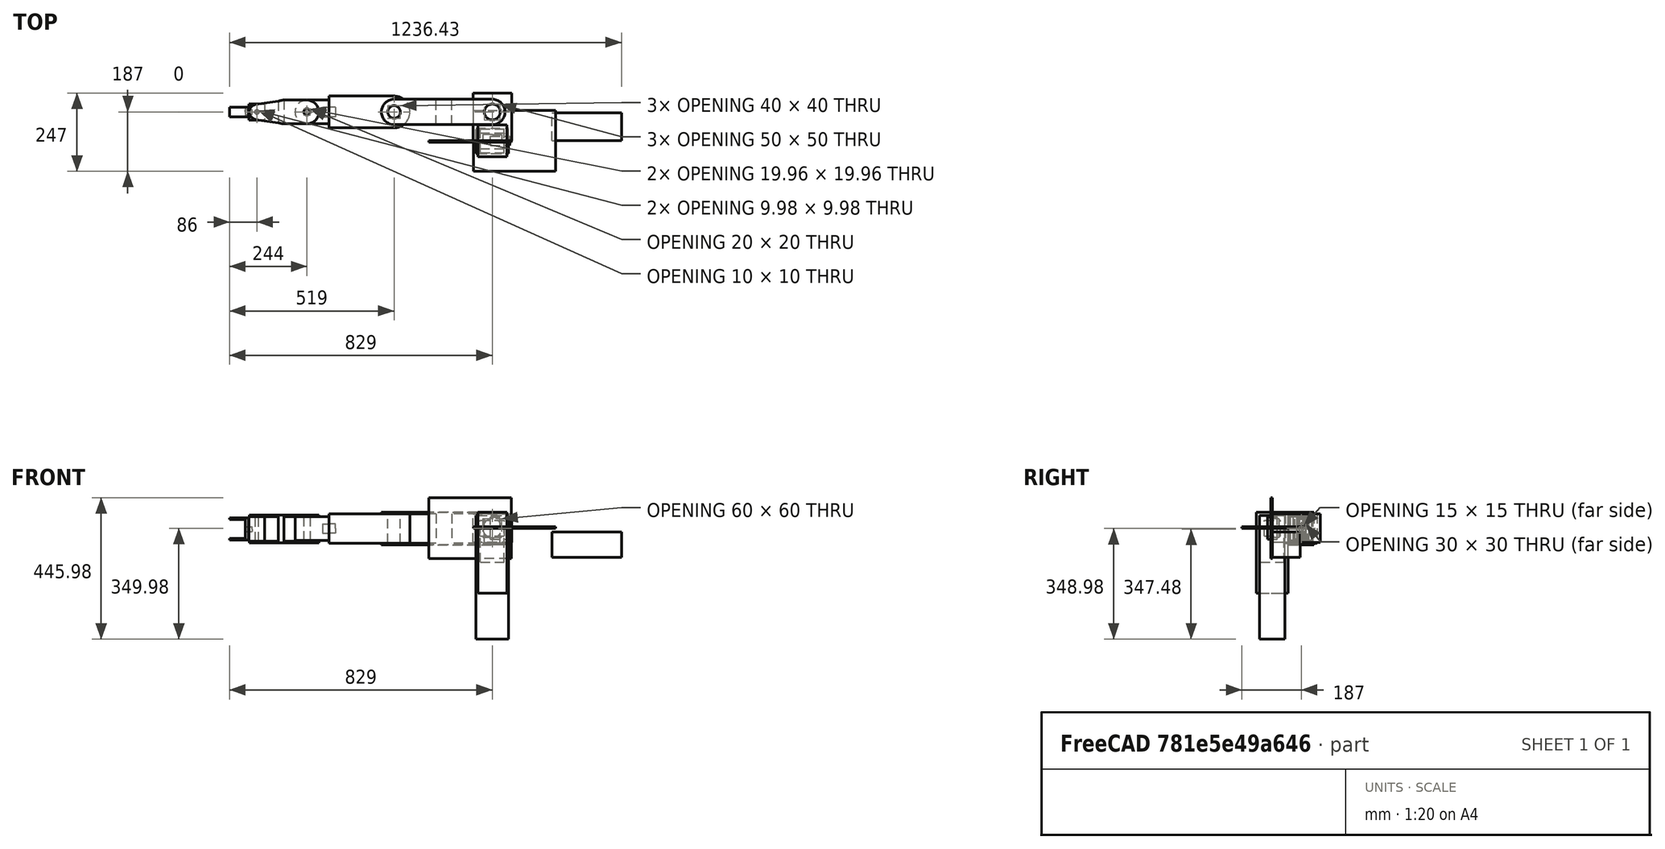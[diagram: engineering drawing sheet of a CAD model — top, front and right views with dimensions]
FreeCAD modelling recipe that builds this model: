
FCSTD DOCUMENT  (FreeCAD 1.0R39109 (Git))
Label: Arm_CAD
License: All rights reserved
LicenseURL: https://en.wikipedia.org/wiki/All_rights_reserved
objects: App::Link×24, App::Part×17, App::FeaturePython×15, Part::Feature×8, Part::Box×8, App::DocumentObjectGroup×1, App::DocumentObjectGroupPython×1
note: 16 computed .brp shape members not serialized (recipe doc carries the construction recipe); baked Part::Feature solids carry a one-line shape summary decoded from their .brp

FEATURE [Part::Feature] Part__Feature  label="Link0"
  shape: bbox 122 x 151 x 90 mm, 11 faces (baked)
FEATURE [Part::Feature] Part__Feature001  label="Link1"
  Placement = pos=(2.26e-14,91,-1.25) rot=(0,1,0;1.5708rad)
  shape: bbox 390 x 80 x 102.5 mm, 24 faces (baked)
FEATURE [Part::Feature] Part__Feature002  label="Link2"
  Placement = pos=(-310,91,-1) rot=(0.707107,0,0.707107;3.14159rad)
  shape: bbox 255 x 100 x 92 mm, 12 faces (baked)
FEATURE [Part::Feature] Part__Feature003  label="Link3"
  Placement = pos=(-515,91,-1) rot=(0,1,0;1.5708rad)
  shape: bbox 107.5 x 75 x 75 mm, 11 faces (baked)
FEATURE [Part::Feature] Part__Feature004  label="Base"
  Placement = pos=(-1.822e-13,-5,-2.788e-13) rot=(0,0.707107,0.707107;3.14159rad)
  shape: bbox 260 x 5 x 192 mm, 8 faces (baked)
FEATURE [Part::Feature] Part__Feature005  label="Link4"
  Placement = pos=(-957.544,122.197,41.5) rot=(-0.999068,-0.030524,0.030524;1.57173rad)
  shape: bbox 219.5 x 75 x 88 mm, 36 faces (baked)
FEATURE [Part::Feature] Part__Feature006  label="Link5"
  Placement = pos=(-743,91,-2.5) rot=(0,1,0;1.5708rad)
  shape: bbox 50 x 50 x 78 mm, 11 faces (baked)
FEATURE [Part::Feature] Part__Feature007  label="Claw"
  Placement = pos=(-774,91,-2.5) rot=(0,1,0;3.14159rad)
  shape: bbox 61 x 30 x 70 mm, 16 faces (baked)
FEATURE [App::Link] Base001  label="Base002"
  LinkedObject = -> Part__Feature004
FEATURE [App::Part] Base  label="Base001"
  Group = -> [Base001]
  Origin = -> Origin001
FEATURE [App::Link] real_l_Base001_
  LinkedObject = -> Base
FEATURE [App::Link] Link001
  LinkedObject = -> Part__Feature
FEATURE [App::Part] Link0  label="Link006"
  Group = -> [Link001]
  Origin = -> Origin002
FEATURE [App::Link] Link002
  LinkedObject = -> Part__Feature001
FEATURE [App::Part] Link1  label="Link007"
  Group = -> [Link002]
  Origin = -> Origin003
FEATURE [App::Link] Link003
  LinkedObject = -> Part__Feature002
FEATURE [App::Part] Link2  label="Link008"
  Group = -> [Link003]
  Origin = -> Origin004
FEATURE [App::Link] Link004
  LinkedObject = -> Part__Feature003
FEATURE [App::Part] Link3  label="Link009"
  Group = -> [Link004]
  Origin = -> Origin005
FEATURE [App::Link] Link005
  LinkedObject = -> Part__Feature005
FEATURE [App::Part] Link4  label="Link010"
  Group = -> [Link005]
  Origin = -> Origin006
FEATURE [App::Link] Link006  label="Link012"
  LinkedObject = -> Part__Feature006
FEATURE [App::Part] Link5  label="Link011"
  Group = -> [Link006]
  Origin = -> Origin007
FEATURE [App::Link] Claw001  label="Claw002"
  LinkedObject = -> Part__Feature007
FEATURE [App::Part] Claw  label="Claw001"
  Group = -> [Claw001]
  Origin = -> Origin008
FEATURE [App::Part] _X2_88c5914d4f53_X0_  label="Arm_asm"
  Group = -> [Part__Feature007,Part__Feature006,Part__Feature005,Part__Feature003,Part__Feature002,Part__Feature001,Part__Feature,Part__Feature004,Base,Link0,Link1,Link2,Link3,Link4,Link5,Claw]
  Origin = -> Origin
FEATURE [App::FeaturePython] l_Base001__to__l_Link006  # WARN: FeaturePython — macro-defined, semantics opaque (R4)
  Child = 1
  Effort = 0
  JoinRotationDirection = 0
  JointSpecific = 0
  LowerLimit = -180
  Mimic = false
  Multiplier = 1
  Origin = pos=(-6e-16,9e-16,5) rot=(1,0,0;3.14159rad)
  Parent = 1
  Placement = pos=(-6e-16,9e-16,5) rot=(1,0,0;3.14159rad)
  Position = 0
  Type = 2
  UpperLimit = 180
  Velocity = 180
  _Type = Cross::Joint
FEATURE [App::FeaturePython] l_Link006__to__l_Link007  # WARN: FeaturePython — macro-defined, semantics opaque (R4)
  Child = 1
  Effort = 0
  JoinRotationDirection = 0
  JointSpecific = 0
  LowerLimit = -90
  Mimic = false
  Multiplier = 1
  Origin = pos=(0,45,-91) rot=(-1,0,0;4.71239rad)
  Parent = 2
  Placement = pos=(1.76e-14,-45,96) rot=(-1,0,0;1.5708rad)
  Position = 0
  Type = 2
  UpperLimit = 90
  Velocity = 180
  _Type = Cross::Joint
FEATURE [App::FeaturePython] l_Link007__to__l_Link008  # WARN: FeaturePython — macro-defined, semantics opaque (R4)
  Child = 1
  Effort = 0
  JoinRotationDirection = 0
  JointSpecific = 0
  LowerLimit = -90
  Mimic = false
  Multiplier = 1
  Origin = pos=(1.67e-14,-310,92.5) rot=(0,-1,0;3.14159rad)
  Parent = 3
  Placement = pos=(9.63e-14,47.5,406) rot=(0,-0.707107,0.707107;3.14159rad)
  Position = 0
  Type = 2
  UpperLimit = 90
  Velocity = 180
  _Type = Cross::Joint
FEATURE [App::FeaturePython] l_Link008__to__l_Link009  # WARN: FeaturePython — macro-defined, semantics opaque (R4)
  Child = 1
  Effort = 0
  JoinRotationDirection = 0
  JointSpecific = 0
  LowerLimit = -180
  Mimic = false
  Multiplier = 1
  Origin = pos=(1.4133e-12,-205,46) rot=(-0.57735,-0.57735,-0.57735;2.0944rad)
  Parent = 4
  Placement = pos=(-1.3841e-12,1.5,611) rot=(0.707107,-0.707107,0;3.14159rad)
  Position = 0
  Type = 2
  UpperLimit = 180
  Velocity = 180
  _Type = Cross::Joint
FEATURE [App::FeaturePython] l_Link009__to__l_Link010  # WARN: FeaturePython — macro-defined, semantics opaque (R4)
  Child = 1
  Effort = 0
  JoinRotationDirection = 0
  JointSpecific = 0
  LowerLimit = -180
  Mimic = false
  Multiplier = 1
  Origin = pos=(37.5,-4.277e-13,-70) rot=(-0.57735,-0.57735,0.57735;2.0944rad)
  Parent = 5
  Placement = pos=(-1.4753e-12,-36,681) rot=(0,-0.707107,-0.707107;3.14159rad)
  Position = 0
  Type = 2
  UpperLimit = 0
  Velocity = 180
  _Type = Cross::Joint
FEATURE [App::FeaturePython] l_Link010__to__l_Link011  # WARN: FeaturePython — macro-defined, semantics opaque (R4)
  Child = 1
  Effort = 0
  JoinRotationDirection = 0
  JointSpecific = 0
  LowerLimit = -90
  Mimic = false
  Multiplier = 1
  Origin = pos=(-157.705,-9.64567,78) rot=(0,0,1;0rad)
  Parent = 6
  Placement = pos=(157.705,42,671.354) rot=(0,-0.707107,-0.707107;3.14159rad)
  Position = 0
  Type = 2
  UpperLimit = 90
  Velocity = 180
  _Type = Cross::Joint
FEATURE [App::FeaturePython] l_Link011__to__l_Claw001  # WARN: FeaturePython — macro-defined, semantics opaque (R4)
  Child = 1
  Effort = 0
  JoinRotationDirection = 0
  JointSpecific = 0
  LowerLimit = -180
  Mimic = false
  Multiplier = 1
  Origin = pos=(-25,-3.411e-13,-39) rot=(0.707107,0,0.707107;3.14159rad)
  Parent = 7
  Placement = pos=(182.705,3,671.354) rot=(-0.57735,-0.57735,0.57735;2.0944rad)
  Position = 0
  Type = 2
  UpperLimit = 180
  Velocity = 180
  _Type = Cross::Joint
FEATURE [App::Link] real_l_Claw001_
  LinkPlacement = pos=(188.705,3,671.354) rot=(-1,0,0;1.5708rad)
  LinkedObject = -> Claw
  Placement = pos=(188.705,3,671.354) rot=(-1,0,0;1.5708rad)
FEATURE [App::Link] real_l_Link011_
  LinkPlacement = pos=(157.705,3,671.354) rot=(-0.57735,-0.57735,0.57735;2.0944rad)
  LinkedObject = -> Link5
  Placement = pos=(157.705,3,671.354) rot=(-0.57735,-0.57735,0.57735;2.0944rad)
FEATURE [App::Link] real_l_Link010_
  LinkPlacement = pos=(369.945,-41,627.118) rot=(0,-1,0;3.14159rad)
  LinkedObject = -> Link4
  Placement = pos=(369.945,-41,627.118) rot=(0,-1,0;3.14159rad)
FEATURE [App::Link] real_l_Link009_
  LinkPlacement = pos=(-9.294e-13,1.5,611) rot=(0.707107,-0.707107,0;3.14159rad)
  LinkedObject = -> Link3
  Placement = pos=(-9.294e-13,1.5,611) rot=(0.707107,-0.707107,0;3.14159rad)
FEATURE [App::Link] real_l_Link008_
  LinkPlacement = pos=(6e-14,1.5,406) rot=(0.707107,-0.707107,0;3.14159rad)
  LinkedObject = -> Link2
  Placement = pos=(6e-14,1.5,406) rot=(0.707107,-0.707107,0;3.14159rad)
FEATURE [App::Link] real_l_Link007_
  LinkPlacement = pos=(3.81e-14,1.25,96) rot=(-0.707107,-0.707107,0;3.14159rad)
  LinkedObject = -> Link1
  Placement = pos=(3.81e-14,1.25,96) rot=(-0.707107,-0.707107,0;3.14159rad)
FEATURE [App::Link] real_l_Link006_
  LinkPlacement = pos=(-6e-16,9e-16,5) rot=(1,0,0;1.5708rad)
  LinkedObject = -> Link0
  Placement = pos=(-6e-16,9e-16,5) rot=(1,0,0;1.5708rad)
FEATURE [Part::Box] col_Base__BoundBox
  AttacherType = Attacher::AttachEngine3D
  Height = 5
  Length = 260
  Placement = pos=(-60,-96,-9e-16) rot=(0,0,1;0rad)
  Width = 192
FEATURE [App::Part] col__l_Base001__col_Base__BoundBox
  Group = -> [col_Base__BoundBox]
  Origin = -> Origin009
FEATURE [App::Link] collision_l_Base001_
  LinkedObject = -> col__l_Base001__col_Base__BoundBox
FEATURE [App::FeaturePython] l_Base001  # WARN: FeaturePython — macro-defined, semantics opaque (R4)
  CalculateInertiaBasedOnMass = false
  Collision = -> [col__l_Base001__col_Base__BoundBox]
  Group = -> [real_l_Base001_,collision_l_Base001_]
  Ixx = 0
  Ixy = 0
  Ixz = 0
  Iyy = 0
  Iyz = 0
  Izz = 0
  Mass = 0
  MaterialNotCalculate = false
  Real = -> [Base]
  Visual = -> [Base]
  _Type = Cross::Link
FEATURE [Part::Box] col_Link0__BoundBox
  AttacherType = Attacher::AttachEngine3D
  Height = 90
  Length = 122
  Placement = pos=(-61,0,-45) rot=(0,0,1;0rad)
  Width = 151
FEATURE [App::Part] col__l_Link006__col_Link0__BoundBox
  Group = -> [col_Link0__BoundBox]
  Origin = -> Origin010
  Placement = pos=(-6e-16,9e-16,5) rot=(1,0,0;1.5708rad)
FEATURE [App::Link] collision_l_Link006_
  LinkPlacement = pos=(-6e-16,9e-16,5) rot=(1,0,0;1.5708rad)
  LinkedObject = -> col__l_Link006__col_Link0__BoundBox
  Placement = pos=(-6e-16,9e-16,5) rot=(1,0,0;1.5708rad)
FEATURE [App::FeaturePython] l_Link006  # WARN: FeaturePython — macro-defined, semantics opaque (R4)
  CalculateInertiaBasedOnMass = false
  Collision = -> [col__l_Link006__col_Link0__BoundBox]
  Group = -> [real_l_Link006_,collision_l_Link006_]
  Ixx = 0
  Ixy = 0
  Ixz = 0
  Iyy = 0
  Iyz = 0
  Izz = 0
  Mass = 0
  MaterialNotCalculate = false
  MountedPlacement = pos=(0,0,0) rot=(-1,0,0;1.5708rad)
  Placement = pos=(-6e-16,9e-16,5) rot=(1,0,0;1.5708rad)
  Real = -> [Link0]
  Visual = -> [Link0]
  _Type = Cross::Link
FEATURE [Part::Box] col_Link1__BoundBox
  AttacherType = Attacher::AttachEngine3D
  Height = 389.985
  Length = 102.5
  Placement = pos=(-51.25,-40,-349.985) rot=(0,0,1;0rad)
  Width = 80
FEATURE [App::Part] col__l_Link007__col_Link1__BoundBox
  Group = -> [col_Link1__BoundBox]
  Origin = -> Origin011
  Placement = pos=(3.42e-14,1.25,96) rot=(-0.707107,-0.707107,0;3.14159rad)
FEATURE [App::Link] collision_l_Link007_
  LinkPlacement = pos=(3.81e-14,1.25,96) rot=(-0.707107,-0.707107,0;3.14159rad)
  LinkedObject = -> col__l_Link007__col_Link1__BoundBox
  Placement = pos=(3.81e-14,1.25,96) rot=(-0.707107,-0.707107,0;3.14159rad)
FEATURE [App::FeaturePython] l_Link007  # WARN: FeaturePython — macro-defined, semantics opaque (R4)
  CalculateInertiaBasedOnMass = false
  Collision = -> [col__l_Link007__col_Link1__BoundBox]
  Group = -> [real_l_Link007_,collision_l_Link007_]
  Ixx = 0
  Ixy = 0
  Ixz = 0
  Iyy = 0
  Iyz = 0
  Izz = 0
  Mass = 0
  MaterialNotCalculate = false
  MountedPlacement = pos=(2.05e-14,5.1e-15,46.25) rot=(-0.57735,-0.57735,-0.57735;2.0944rad)
  Placement = pos=(3.81e-14,1.25,96) rot=(-0.707107,-0.707107,0;3.14159rad)
  Real = -> [Link1]
  Visual = -> [Link1]
  _Type = Cross::Link
FEATURE [Part::Box] col_Link2__BoundBox
  AttacherType = Attacher::AttachEngine3D
  Height = 255
  Length = 92
  Placement = pos=(-46,-50,-205) rot=(0,0,1;0rad)
  Width = 100
FEATURE [App::Part] col__l_Link008__col_Link2__BoundBox
  Group = -> [col_Link2__BoundBox]
  Origin = -> Origin012
  Placement = pos=(4e-14,1.5,406) rot=(0.707107,-0.707107,0;3.14159rad)
FEATURE [App::Link] collision_l_Link008_
  LinkPlacement = pos=(6e-14,1.5,406) rot=(0.707107,-0.707107,0;3.14159rad)
  LinkedObject = -> col__l_Link008__col_Link2__BoundBox
  Placement = pos=(6e-14,1.5,406) rot=(0.707107,-0.707107,0;3.14159rad)
FEATURE [App::FeaturePython] l_Link008  # WARN: FeaturePython — macro-defined, semantics opaque (R4)
  CalculateInertiaBasedOnMass = false
  Collision = -> [col__l_Link008__col_Link2__BoundBox]
  Group = -> [real_l_Link008_,collision_l_Link008_]
  Ixx = 0
  Ixy = 0
  Ixz = 0
  Iyy = 0
  Iyz = 0
  Izz = 0
  Mass = 0
  MaterialNotCalculate = false
  MountedPlacement = pos=(1.02e-14,1.02e-14,46) rot=(-0.57735,-0.57735,-0.57735;2.0944rad)
  Placement = pos=(6e-14,1.5,406) rot=(0.707107,-0.707107,0;3.14159rad)
  Real = -> [Link2]
  Visual = -> [Link2]
  _Type = Cross::Link
FEATURE [Part::Box] col_Link3__BoundBox
  AttacherType = Attacher::AttachEngine3D
  Height = 107.486
  Length = 75
  Placement = pos=(-37.5,-37.5,-107.486) rot=(0,0,1;0rad)
  Width = 75
FEATURE [App::Part] col__l_Link009__col_Link3__BoundBox
  Group = -> [col_Link3__BoundBox]
  Origin = -> Origin013
  Placement = pos=(-9.405e-13,1.5,611) rot=(0.707107,-0.707107,0;3.14159rad)
FEATURE [App::Link] collision_l_Link009_
  LinkPlacement = pos=(-9.294e-13,1.5,611) rot=(0.707107,-0.707107,0;3.14159rad)
  LinkedObject = -> col__l_Link009__col_Link3__BoundBox
  Placement = pos=(-9.294e-13,1.5,611) rot=(0.707107,-0.707107,0;3.14159rad)
FEATURE [App::FeaturePython] l_Link009  # WARN: FeaturePython — macro-defined, semantics opaque (R4)
  CalculateInertiaBasedOnMass = false
  Collision = -> [col__l_Link009__col_Link3__BoundBox]
  Group = -> [real_l_Link009_,collision_l_Link009_]
  Ixx = 0
  Ixy = 0
  Ixz = 0
  Iyy = 0
  Iyz = 0
  Izz = 0
  Mass = 0
  MaterialNotCalculate = false
  MountedPlacement = pos=(-4.547e-13,-4.547e-13,-4.547e-13) rot=(0,0,1;0rad)
  Placement = pos=(-9.294e-13,1.5,611) rot=(0.707107,-0.707107,0;3.14159rad)
  Real = -> [Link3]
  Visual = -> [Link3]
  _Type = Cross::Link
FEATURE [Part::Box] col_Link4__BoundBox
  AttacherType = Attacher::AttachEngine3D
  Height = 79.411
  Length = 219.194
  Placement = pos=(188.24,0,-91.3824) rot=(0,0,1;0rad)
  Width = 88
FEATURE [App::Part] col__l_Link010__col_Link4__BoundBox
  Group = -> [col_Link4__BoundBox]
  Origin = -> Origin014
  Placement = pos=(369.945,-41,627.118) rot=(0,-1,0;3.14159rad)
FEATURE [App::Link] collision_l_Link010_
  LinkPlacement = pos=(369.945,-41,627.118) rot=(0,-1,0;3.14159rad)
  LinkedObject = -> col__l_Link010__col_Link4__BoundBox
  Placement = pos=(369.945,-41,627.118) rot=(0,-1,0;3.14159rad)
FEATURE [App::FeaturePython] l_Link010  # WARN: FeaturePython — macro-defined, semantics opaque (R4)
  CalculateInertiaBasedOnMass = false
  Collision = -> [col__l_Link010__col_Link4__BoundBox]
  Group = -> [real_l_Link010_,collision_l_Link010_]
  Ixx = 0
  Ixy = 0
  Ixz = 0
  Iyy = 0
  Iyz = 0
  Izz = 0
  Mass = 0
  MaterialNotCalculate = false
  MountedPlacement = pos=(-369.945,-53.8824,-5) rot=(1,0,0;1.5708rad)
  Placement = pos=(369.945,-41,627.118) rot=(0,-1,0;3.14159rad)
  Real = -> [Link4]
  Visual = -> [Link4]
  _Type = Cross::Link
FEATURE [Part::Box] col_Link5__BoundBox
  AttacherType = Attacher::AttachEngine3D
  Height = 50
  Length = 78
  Placement = pos=(-39,-25,-25) rot=(0,0,1;0rad)
  Width = 50
FEATURE [App::Part] col__l_Link011__col_Link5__BoundBox
  Group = -> [col_Link5__BoundBox]
  Origin = -> Origin015
  Placement = pos=(157.705,3,671.354) rot=(-0.57735,-0.57735,0.57735;2.0944rad)
FEATURE [App::Link] collision_l_Link011_
  LinkPlacement = pos=(157.705,3,671.354) rot=(-0.57735,-0.57735,0.57735;2.0944rad)
  LinkedObject = -> col__l_Link011__col_Link5__BoundBox
  Placement = pos=(157.705,3,671.354) rot=(-0.57735,-0.57735,0.57735;2.0944rad)
FEATURE [App::FeaturePython] l_Link011  # WARN: FeaturePython — macro-defined, semantics opaque (R4)
  CalculateInertiaBasedOnMass = false
  Collision = -> [col__l_Link011__col_Link5__BoundBox]
  Group = -> [real_l_Link011_,collision_l_Link011_]
  Ixx = 0
  Ixy = 0
  Ixz = 0
  Iyy = 0
  Iyz = 0
  Izz = 0
  Mass = 0
  MaterialNotCalculate = false
  MountedPlacement = pos=(-2.36e-13,-3.324e-13,-39) rot=(0.707107,0,0.707107;3.14159rad)
  Placement = pos=(157.705,3,671.354) rot=(-0.57735,-0.57735,0.57735;2.0944rad)
  Real = -> [Link5]
  Visual = -> [Link5]
  _Type = Cross::Link
FEATURE [Part::Box] col_Claw__BoundBox
  AttacherType = Attacher::AttachEngine3D
  Height = 70
  Length = 61
  Placement = pos=(-6,-15,-35) rot=(0,0,1;0rad)
  Width = 30
FEATURE [App::Part] col__l_Claw001__col_Claw__BoundBox
  Group = -> [col_Claw__BoundBox]
  Origin = -> Origin016
  Placement = pos=(188.705,3,671.354) rot=(-1,0,0;1.5708rad)
FEATURE [App::DocumentObjectGroup] Collisions
  Group = -> [col__l_Base001__col_Base__BoundBox,col__l_Link006__col_Link0__BoundBox,col__l_Link007__col_Link1__BoundBox,col__l_Link008__col_Link2__BoundBox,col__l_Link009__col_Link3__BoundBox,col__l_Link010__col_Link4__BoundBox,col__l_Link011__col_Link5__BoundBox,col__l_Claw001__col_Claw__BoundBox]
FEATURE [App::Link] collision_l_Claw001_
  LinkPlacement = pos=(188.705,3,671.354) rot=(-1,0,0;1.5708rad)
  LinkedObject = -> col__l_Claw001__col_Claw__BoundBox
  Placement = pos=(188.705,3,671.354) rot=(-1,0,0;1.5708rad)
FEATURE [App::FeaturePython] l_Claw001  # WARN: FeaturePython — macro-defined, semantics opaque (R4)
  CalculateInertiaBasedOnMass = false
  Collision = -> [col__l_Claw001__col_Claw__BoundBox]
  Group = -> [real_l_Claw001_,collision_l_Claw001_]
  Ixx = 0
  Ixy = 0
  Ixz = 0
  Iyy = 0
  Iyz = 0
  Izz = 0
  Mass = 0
  MaterialNotCalculate = false
  MountedPlacement = pos=(-3.404e-13,-4.537e-13,-6) rot=(0,1,0;1.5708rad)
  Placement = pos=(188.705,3,671.354) rot=(-1,0,0;1.5708rad)
  Real = -> [Claw]
  Visual = -> [Claw]
  _Type = Cross::Link
FEATURE [App::DocumentObjectGroupPython] Robot  # scripted group (container) (typed FeaturePython)
  GenerateCodeForRosVersion = 0
  Group = -> [l_Base001,l_Link006,l_Link007,l_Link008,l_Link009,l_Link010,l_Link011,l_Claw001,l_Base001__to__l_Link006,l_Link006__to__l_Link007,l_Link007__to__l_Link008,l_Link008__to__l_Link009,l_Link009__to__l_Link010,l_Link010__to__l_Link011,l_Link011__to__l_Claw001]
  Mass = 0
  RobotType = 0
  _Type = Cross::Robot
  l_Base001__to__l_Link006_deg = 0
  l_Link006__to__l_Link007_deg = 0
  l_Link007__to__l_Link008_deg = 0
  l_Link008__to__l_Link009_deg = 0
  l_Link009__to__l_Link010_deg = 0
  l_Link010__to__l_Link011_deg = 0
  l_Link011__to__l_Claw001_deg = 0
